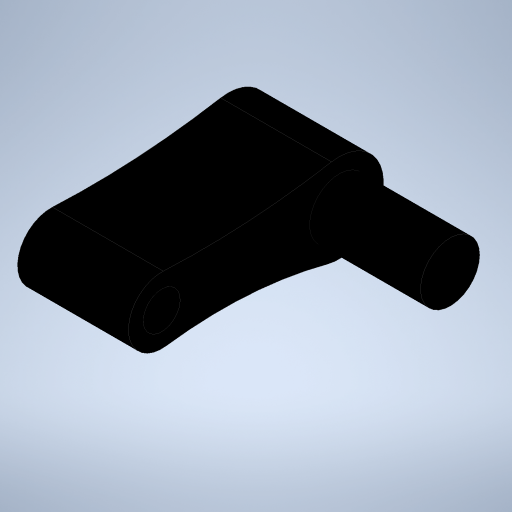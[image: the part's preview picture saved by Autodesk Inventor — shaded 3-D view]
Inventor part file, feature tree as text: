
AUTODESK INVENTOR PART (.ipt)
format: ipt  version: 2023 (Build 270158000, 158)  size: 256,512 bytes
history: native  units: mm
features: extrude x2, sketch x2
ambient origin geometry x8: Origin, YZ Plane, XZ Plane, XY Plane, X Axis, Y Axis, Z Axis, Center Point
bodies: Volumenkörper1 (feature_tree)
feature tree (4):
  extrude  "Extrusion1"  Depth=9.0mm
  extrude  "Extrusion2"  Depth=9.0mm
  sketch  "Skizze1"  dims[d0=9.0mm d1=12.0mm]
  sketch  "Skizze2"  dims[d2=15.0mm d3=9.0mm d4=0.0mm d5=0.0mm d6=5.0mm d8=15.0mm d9=0.0mm d10=8.0mm d11=15.0mm d12=0.0mm]
